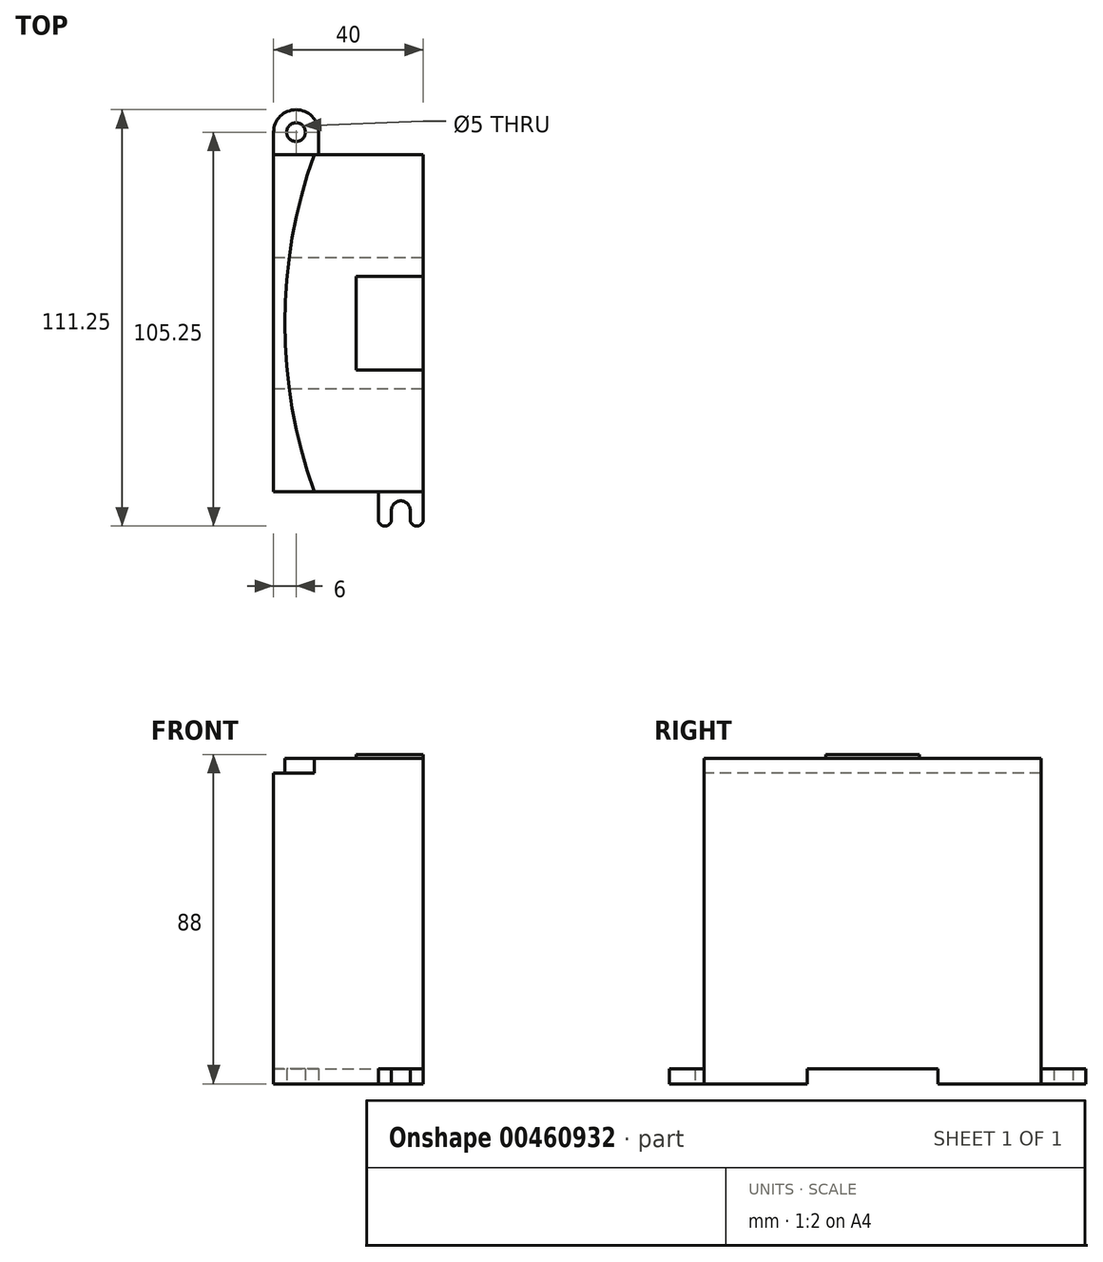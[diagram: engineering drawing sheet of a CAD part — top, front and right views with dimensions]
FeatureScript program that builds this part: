
annotation { "Feature Type Name" : "Feature", "Feature Type Description" : "" }
export const myFeature = defineFeature(function(context is Context, id is Id, definition is map)
    precondition{}
    {
        {
            var Q0;
            Q0=qCreatedBy(makeId("Top.planeOp"),FACE);
            var sketch = newSketch(context, id + "F0", { "sketchPlane" : qUnion([Q0])});
            skLineSegment(sketch, "E0.bottom", {"start": v(20, 45) * mm, "end": v(-20, 45) * mm});
            skLineSegment(sketch, "E0.top", {"start": v(20, -45) * mm, "end": v(-20, -45) * mm});
            skLineSegment(sketch, "E0.left", {"start": v(20, 45) * mm, "end": v(20, -45) * mm});
            skLineSegment(sketch, "E0.right", {"start": v(-20, 45) * mm, "end": v(-20, -45) * mm});
            skPoint(sketch, "E0.middle", {"position": v(0, 0) * mm});
            skLineSegment(sketch, "E1", {"start": v(-20, 45) * mm, "end": v(-20, 51) * mm});
            skLineSegment(sketch, "E2", {"start": v(-8, 45) * mm, "end": v(-8, 51) * mm});
            skArc(sketch, "E3", {"start": v(-8, 51) * mm, "mid": v(-14, 57) * mm, "end": v(-20, 51) * mm});
            skCircle(sketch, "E4", {"center": v(-14, 51) * mm, "radius": 2.5 * mm});
            skLineSegment(sketch, "E5", {"start": v(20, -45) * mm, "end": v(20, -52.5) * mm});
            skArc(sketch, "E6", {"start": v(16.5, -52.5) * mm, "mid": v(18.25, -54.25) * mm, "end": v(20, -52.5) * mm});
            skLineSegment(sketch, "E7", {"start": v(20, -52.5) * mm, "end": v(8, -52.5) * mm, "construction": true});
            skLineSegment(sketch, "E8", {"start": v(8, -52.5) * mm, "end": v(8, -45) * mm});
            skArc(sketch, "E9", {"start": v(8, -52.5) * mm, "mid": v(9.75, -54.25) * mm, "end": v(11.5, -52.5) * mm});
            skLineSegment(sketch, "E10", {"start": v(11.5, -52.5) * mm, "end": v(11.5, -50) * mm});
            skLineSegment(sketch, "E11", {"start": v(16.5, -52.5) * mm, "end": v(16.5, -50) * mm});
            skArc(sketch, "E12", {"start": v(16.5, -50) * mm, "mid": v(14, -47.5) * mm, "end": v(11.5, -50) * mm});
            skSolve(sketch);
        }
        {
            var Q0;
            {var subQ3=sQuery(id+"F0.wireOp",EDGE,"E0.left");Q0=makeQuery(id+"F0.imprint","IMPRINT",FACE,{"disambiguationData":[TD([[makeQuery(id+"F0.imprint","IMPRINT",EDGE,{"derivedFrom":subQ3}),-1.0]])]});}
            extrude(context, id + "F1", {"entities" : qUnion([Q0]), "depth" : 87 * mm, "offsetDistance" : 25 * mm});
        }
        {
            var Q0;
            {var subQ1=sQuery(id+"F0.wireOp",EDGE,"E1");Q0=makeQuery(id+"F0.imprint","IMPRINT",FACE,{"disambiguationData":[TD([[makeQuery(id+"F0.imprint","IMPRINT",EDGE,{"derivedFrom":subQ1}),-1.0]])]});}
            var Q1;
            {var subQ0=sQuery(id+"F0.wireOp",EDGE,"E5");Q1=makeQuery(id+"F0.imprint","IMPRINT",FACE,{"disambiguationData":[TD([[makeQuery(id+"F0.imprint","IMPRINT",EDGE,{"derivedFrom":subQ0}),-1.0]])]});}
            extrude(context, id + "F2", {"entities" : qUnion([Q0, Q1]), "depth" : 4 * mm, "offsetDistance" : 25 * mm});
        }
        {
            var Q0;
            Q0=makeQuery(id+"F1.opExtrude","CAP_FACE",FACE,{"disambiguationData":[OSD([sQuery(id+"F0.wireOp",EDGE,"E0.bottom"),sQuery(id+"F0.wireOp",EDGE,"E0.top"),sQuery(id+"F0.wireOp",EDGE,"E0.left"),sQuery(id+"F0.wireOp",EDGE,"E0.right")])],"isStart":false});
            var sketch = newSketch(context, id + "F3", { "sketchPlane" : qUnion([Q0])});
            skArc(sketch, "E13", {"start": v(-9.16, 45) * mm, "mid": v(-17, 0) * mm, "end": v(-9.16, -45) * mm});
            skLineSegment(sketch, "E14", {"start": v(-9.16, 45) * mm, "end": v(-9.16, -45) * mm, "construction": true});
            skLineSegment(sketch, "E15", {"start": v(-9.16, 45) * mm, "end": v(-9.16, 62.9) * mm});
            skLineSegment(sketch, "E16", {"start": v(-9.16, 62.9) * mm, "end": v(-46.15, 62.9) * mm});
            skLineSegment(sketch, "E17", {"start": v(-46.15, 62.9) * mm, "end": v(-46.15, -56.39) * mm});
            skLineSegment(sketch, "E18", {"start": v(-46.15, -56.39) * mm, "end": v(-9.16, -56.39) * mm});
            skLineSegment(sketch, "E19", {"start": v(-9.16, -56.39) * mm, "end": v(-9.16, -45) * mm});
            skSolve(sketch);
        }
        {
            var Q0;
            {var subQ0=sQuery(id+"F3.wireOp",EDGE,"E15");Q0=makeQuery(id+"F3.imprint","IMPRINT",FACE,{"disambiguationData":[TD([[makeQuery(id+"F3.imprint","IMPRINT",EDGE,{"derivedFrom":subQ0}),1.0]])]});}
            var Q1;
            {var subQ0=sQuery(id+"F3.wireOp",EDGE,"E13");Q1=makeQuery(id+"F3.imprint","IMPRINT",FACE,{"disambiguationData":[TD([[makeQuery(id+"F3.imprint","IMPRINT",EDGE,{"derivedFrom":subQ0}),-1.0]])]});}
            extrude(context, id + "F4", {"entities" : qUnion([Q0, Q1]), "operationType" : NewBodyOperationType.REMOVE, "oppositeDirection" : true, "depth" : 4 * mm, "offsetDistance" : 25 * mm});
        }
        {
            var Q0;
            Q0=makeQuery(id+"F1.opExtrude","CAP_FACE",FACE,{"disambiguationData":[OSD([sQuery(id+"F0.wireOp",EDGE,"E0.bottom"),sQuery(id+"F0.wireOp",EDGE,"E0.top"),sQuery(id+"F0.wireOp",EDGE,"E0.left"),sQuery(id+"F0.wireOp",EDGE,"E0.right")])],"isStart":false});
            var sketch = newSketch(context, id + "F5", { "sketchPlane" : qUnion([Q0])});
            skLineSegment(sketch, "E20.bottom", {"start": v(20, -12.5) * mm, "end": v(2, -12.5) * mm});
            skLineSegment(sketch, "E20.top", {"start": v(20, 12.5) * mm, "end": v(2, 12.5) * mm});
            skLineSegment(sketch, "E20.left", {"start": v(20, -12.5) * mm, "end": v(20, 12.5) * mm});
            skLineSegment(sketch, "E20.right", {"start": v(2, -12.5) * mm, "end": v(2, 12.5) * mm});
            skSolve(sketch);
        }
        {
            var Q0;
            Q0=makeQuery(id+"F5.imprint","IMPRINT",FACE,{"disambiguationData":[TD([[makeQuery(id+"F5.imprint","IMPRINT",EDGE,{"derivedFrom":sQuery(id+"F5.wireOp",EDGE,"E20.bottom")}),-1.0]])]});
            extrude(context, id + "F6", {"entities" : qUnion([Q0]), "depth" : 1 * mm, "offsetDistance" : 25 * mm});
        }
        {
            var Q0;
            Q0=makeQuery(id+"F1.opExtrude","SWEPT_FACE",FACE,{"disambiguationData":[OSD([sQuery(id+"F0.wireOp",EDGE,"E0.left")])]});
            var sketch = newSketch(context, id + "F7", { "sketchPlane" : qUnion([Q0])});
            skLineSegment(sketch, "E21.bottom", {"start": v(-17.5, 0) * mm, "end": v(17.5, 0) * mm});
            skLineSegment(sketch, "E21.top", {"start": v(-17.5, 4) * mm, "end": v(17.5, 4) * mm});
            skLineSegment(sketch, "E21.left", {"start": v(-17.5, 0) * mm, "end": v(-17.5, 4) * mm});
            skLineSegment(sketch, "E21.right", {"start": v(17.5, 0) * mm, "end": v(17.5, 4) * mm});
            skSolve(sketch);
        }
        {
            var Q0;
            Q0=makeQuery(id+"F7.imprint","IMPRINT",FACE,{"disambiguationData":[TD([[makeQuery(id+"F7.imprint","IMPRINT",EDGE,{"derivedFrom":sQuery(id+"F7.wireOp",EDGE,"E21.bottom")}),-1.0]])]});
            extrude(context, id + "F8", {"entities" : qUnion([Q0]), "operationType" : NewBodyOperationType.REMOVE, "endBound" : BoundingType.THROUGH_ALL, "oppositeDirection" : true, "depth" : 25 * mm, "offsetDistance" : 25 * mm});
        }
    });
